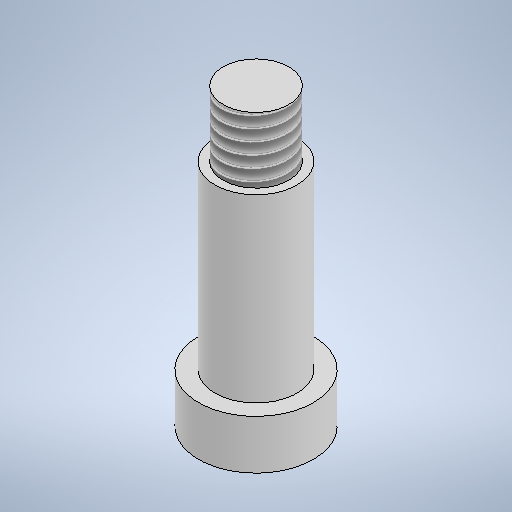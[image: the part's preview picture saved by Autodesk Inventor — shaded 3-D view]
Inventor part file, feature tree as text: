
AUTODESK INVENTOR PART (.ipt)
format: ipt  version: 2025 (Build 290162010, 162A)  size: 266,752 bytes
history: native  units: mm
features: revolve x1, thread x1, sketch x1
ambient origin geometry x8: Origin, YZ Plane, XZ Plane, XY Plane, X Axis, Y Axis, Z Axis, Center Point
bodies: Solid1 (feature_tree)
feature tree (3):
  revolve  "Revolution1"  [1 undecoded]
  thread  "Thread1"  [1 undecoded]
  sketch  "Sketch1"  dims[d0=3.0mm d1=11.0mm d2=4.0mm d3=7.0mm d4=5.0mm d5=4.0mm d6=90.0deg d7=12.0mm d8=0.0mm]
note: 2 required parameter values undecoded (feature->parameter linkage not recoverable at this tier; creation-order binding heuristic only, values carry confidence <= 0.55)